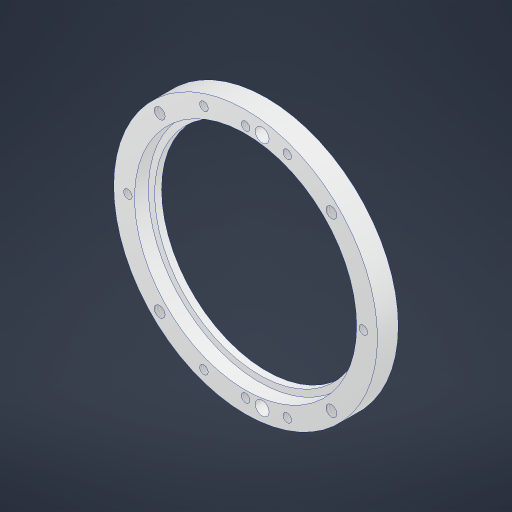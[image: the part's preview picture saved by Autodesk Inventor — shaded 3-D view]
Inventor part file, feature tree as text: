
AUTODESK INVENTOR PART (.ipt)
format: ipt  version: 2023.4 (Build 274418000, 418)  size: 401,920 bytes
history: native  units: in
note: dims shown in document units (in); Inventor stores cm internally (conversion verified against a paired STEP export)
features: sketch x7, hole x4, extrude x3, projected_geometry x1
ambient origin geometry x8: Origin, YZ Plane, XZ Plane, XY Plane, X Axis, Y Axis, Z Axis, Center Point
bodies: Solid1 (feature_tree)
feature tree (15):
  extrude  "Extrusion1"  Depth=0.5in
  extrude  "Extrusion2"  Depth=0.375in
  hole  "Hole1"  [1 undecoded]
  extrude  "Extrusion3"  Depth=0.25in
  hole  "Hole2"  [1 undecoded]
  hole  "Hole3"  [1 undecoded]
  hole  "Hole4"  [1 undecoded]
  sketch  "Sketch1"  dims[d0=4.75in d1=0.5in]
  sketch  "Sketch2"  dims[d2=0.375in d3=0.0in d4=4.0in]
  sketch  "Sketch3"  dims[d5=0.25in d6=0.0in d7=2.12in]
  sketch  "Sketch4"  dims[d8=1.5748in d10=360.0deg]
  sketch  "Sketch5"  dims[d12=0.156in d13=0.38in d14=0.375in d15=0.25in d16=0.5635in d17=0.536in d18=0.8108in d19=3.775in]
  sketch  "Sketch6"  dims[d20=0.25in d21=0.0in d22=4.375in]
  sketch  "Sketch7"  dims[d25=0.75in d26=0.75in d27=0.156in d28=0.38in d29=0.119in d30=0.25in d31=0.5635in d32=1.0in d33=0.8108in d34=4.375in d35=45.0deg d36=1.5748in d38=360.0deg d40=0.196in d41=0.5in d42=0.375in d43=0.25in d44=0.5635in d45=1.0in d46=0.8108in d47=4.11in d49=4.3in d50=0.055in d51=0.25in d52=0.75in d53=0.375in d54=0.25in d55=0.5635in d56=1.0in d57=0.8108in]
  projected_geometry  "Projected Loop1"
note: 4 required parameter values undecoded (feature->parameter linkage not recoverable at this tier; creation-order binding heuristic only, values carry confidence <= 0.55)
